# Revit family: Ciak 1.6A
name_source: partatom
category: Lighting Fixtures
revit_build: Autodesk Revit 2017 (Build: 20160225_1515(x64)
units: mm (PartAtom-declared; Revit-internal decimal feet)

## family parameters
Cut with Voids When Loaded = Yes
Host = Face
Light Source = No
Part Type = Normal
Room Calculation Point = Yes
Round Connector Dimension = Use Diameter
Shared = No

## types (5) — shared parameters
Apparent Load Phase 1 = 3 W
Body = L&L_White aluminium
CRI = 90
Code = CK16001 B White; CK16001 N Black
Control system = -
Cutout dimensions = diam. 50 mm
Default Elevation = 1219 mm
Delivered lumen output = 144 lm (3000K, 29°)
Description = indoor recessed
Energy efficiency class = A A+ A++
Features = -
Geometry 1 = Ciak 1.0_Geometry 1
Geometry 2 = Ciak 1.6_mod : Ciak 1.6
Geometry 3 = Ciak 1.0_Geometry 3
Height mm = 22 mm  [stored 0.0721785 ft]
Height void = 19 mm  [stored 0.062336 ft]
Horizontal rotation max = 350.00°
IP = 40
L1 = 11 mm
LED Colour = 3000K (also available: 2700K and 4000K - ref. URL Technical sheet)
Length mm = 46 mm  [stored 0.150919 ft]
Lens = L&L_Lens
Lumen output at source = 157 lm (3000K)
Manufacturer = L&L Luce&Light
Material = body and trim in aluminium
Model = Ciak 1.6
Mounting = recessed (ceiling, shelf, shop window)
No. and type of led = 1 power LED
Notes = -
Power = 2.5W
Power cables = includes 1.5 m PVC cable FROR 2x0.35/0.35 diam. 3.5 m
Power supply = 24Vdc
Power supply unit = not included
Radius void = 25 mm  [stored 0.082021 ft]
Trim = L&L_Black aluminium
URL = https://www.lucelight.it
URL Accessories and power supply units = https://www.lucelight.it
URL Catalogue = https://www.lucelight.it
URL DXF = https://www.lucelight.it
URL Description = https://www.lucelight.it
URL General code = https://www.lucelight.it
URL IES Photometric file = https://www.lucelight.it
URL Image = https://www.lucelight.it
URL Technical sheet = https://www.lucelight.it
Vertical rotation max = 70.00°
Voltage = 24 V
Weight kg = 0.07
Width mm = 46 mm  [stored 0.150919 ft]
Wiring = parallel

## per-type parameters (varying)
| type | Light Source | Optics |
| Ciak 1.6_L 52° (3000K 2.5W 24Vdc) | Light Source_1.6 : L52° | 52° |
| Ciak 1.6_M 29° (3000K 2.5W 24Vdc) | Light Source_1.6 : M29° | 29° |
| Ciak 1.6_P 48° (3000K 2.5W 24Vdc) | Light Source_1.6 : P48° | 48° |
| Ciak 1.6_S 17° (3000K 2.5W 24Vdc) | Light Source_1.6 : S17° | 17° |
| Ciak 1.6_W 16°x34° (3000K 2.5W 24Vdc) | Light Source_1.6 : W16°x34° | 16°x34° |

note: [stored X ft] marks values corroborated as IEEE doubles in the binary element streams (Revit-internal decimal feet)

## geometry (parser evidence)
native form markers: Blend x2, Extrusion x6, Sweep x20
no freeform markers — native parametric forms only
